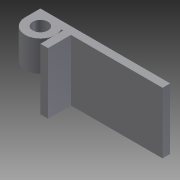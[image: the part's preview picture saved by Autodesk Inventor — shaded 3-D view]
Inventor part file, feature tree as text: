
AUTODESK INVENTOR PART (.ipt)
format: ipt  version: 2011 (Build 150239000, 239)  size: 142,336 bytes
history: native  units: in
note: dims shown in document units (in); Inventor stores cm internally (conversion verified against a paired STEP export)
features: extrude x8, sketch x8
ambient origin geometry x8: Origin, YZ Plane, XZ Plane, XY Plane, X Axis, Y Axis, Z Axis, Center Point
bodies: Solid1 (feature_tree)
feature tree (16):
  extrude  "Extrusion1"  Depth=1.0in
  extrude  "Extrusion2"  Depth=0.125in
  extrude  "Extrusion3"  Depth=0.5in TaperAngle=0.0deg
  extrude  "Extrusion4"  Depth=0.5in TaperAngle=0.0deg
  extrude  "Extrusion5"  Depth=0.125in
  extrude  "Extrusion6"  Depth=0.5in TaperAngle=0.0deg
  extrude  "Extrusion7"  Depth=0.25in
  extrude  "Extrusion8"  Depth=0.375in
  sketch  "Sketch1"  dims[d0=2.0in d1=1.0in]
  sketch  "Sketch2"  dims[d2=0.125in d3=0.0in d4=0.125in]
  sketch  "Sketch3"  dims[d5=0.125in d6=0.5in d7=0.0in]
  sketch  "Sketch4"  dims[d8=0.5in d9=0.0in d10=0.5in d11=0.0in]
  sketch  "Sketch5"  dims[d12=1.0in d13=0.0in d14=0.125in]
  sketch  "Sketch6"  dims[d15=0.125in d16=0.5in d17=0.0in]
  sketch  "Sketch7"  dims[d18=0.5in d19=0.0in d20=0.25in]
  sketch  "Sketch8"  dims[d21=0.125in d22=0.375in d23=0.125in d24=1.0in d25=0.0in]
